# Revit family: 1286xxx Ascoli Single Trimless
name_source: partatom
category: Lighting Fixtures
revit_build: Autodesk Revit 2018 (Build: 20170223_1515(x64)
units: mm (PartAtom-declared; Revit-internal decimal feet)

## family parameters
Always vertical = Yes
Cut with Voids When Loaded = No
Host = Ceiling
Light Source = No
OmniClass Number = 23.80.70.11
OmniClass Title = Luminaries for Internal Lighting
Part Type = Normal
Room Calculation Point = No
Round Connector Dimension = Use Diameter
Shared = No

## types (2) — shared parameters
Dimmable = Yes
Driver Required = No
Efficacy (lm/w) = Lamp Dependent
Electrical Class = I
Lamp = GU10
Light Source Fixed = No
Main Finish = Matt White / Matt Black
Main Material = Aluminium
Manufacturer URL - Europe and Rest of World = www.astrolighting.com
Manufacturer URL - North America = us.astrolighting.com
Product CCT = 2700K / 3000K
zero-valued in all types: Product Weight (KG)

## per-type parameters (varying)
| type | ADA compliant | Dimming Method | Driver Included | Location / IP Rating | Power (Watts) | Product CRI | Product Location | Product Name | Product SKU |
| CE | Not Applicable | Lamp Dependent | Not Applicable | IP20 | 6W Max | 80 / 90 | Interior | Ascoli Trimless | 1286xxx |
| ETL |  | Lamp Depenent |  |  | Max 6W | 80/ 90 |  |  | 1234567 |

## geometry (parser evidence)
native form markers: Sweep x2
no freeform markers — native parametric forms only
